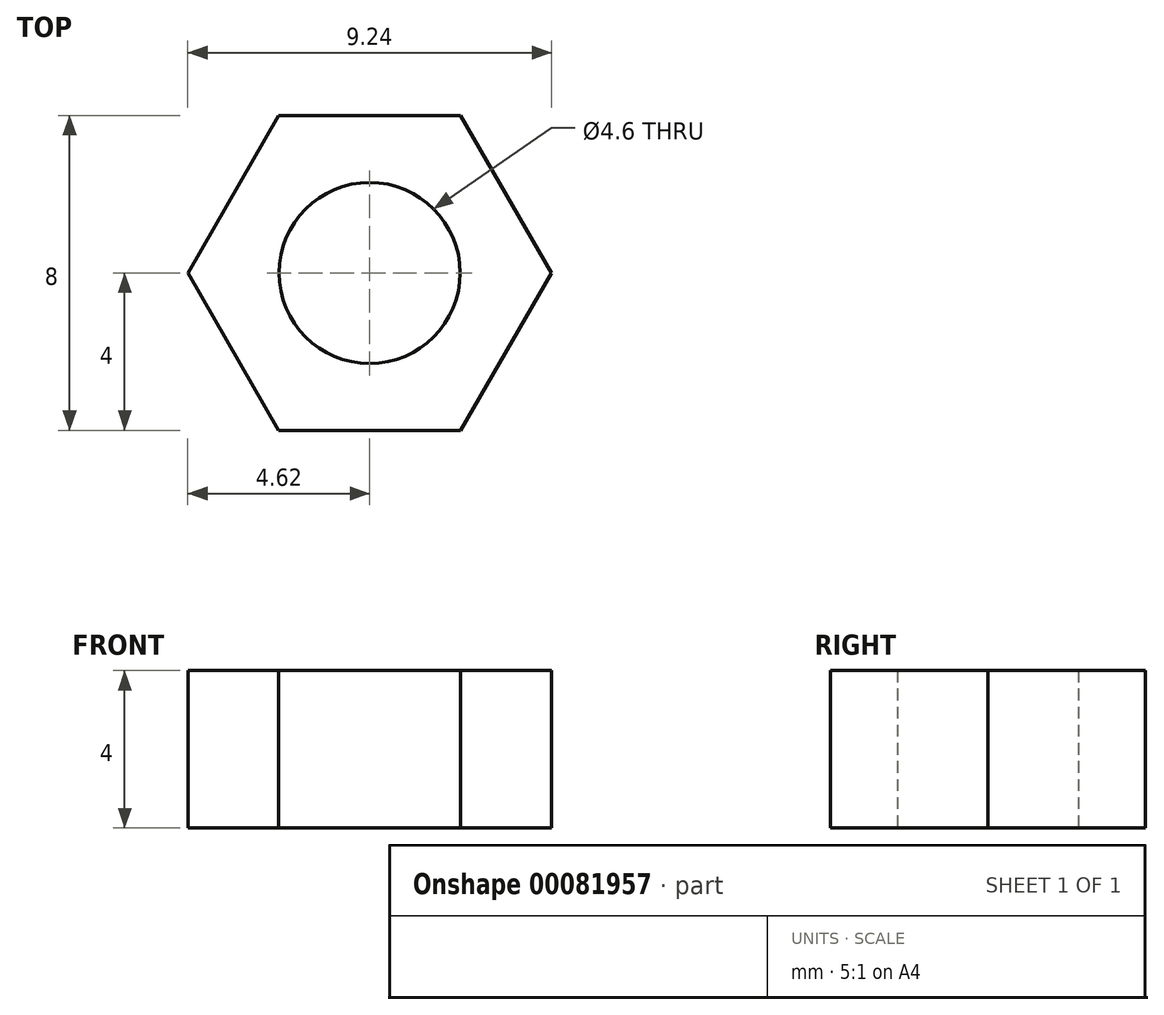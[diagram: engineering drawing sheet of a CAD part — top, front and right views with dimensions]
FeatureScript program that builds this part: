
annotation { "Feature Type Name" : "Feature", "Feature Type Description" : "" }
export const myFeature = defineFeature(function(context is Context, id is Id, definition is map)
    precondition{}
    {
        {
            assignVariable(context, id + "F0", {"name" : "NutT", "anyValue" : 4});
        }
        {
            var Q0;
            Q0=qCreatedBy(makeId("Top.planeOp"),FACE);
            var sketch = newSketch(context, id + "F1", { "sketchPlane" : qUnion([Q0])});
            skCircle(sketch, "E0.cCircle", {"center": v(0, 0) * mm, "radius": 4 * mm, "construction": true});
            skLineSegment(sketch, "E0.0", {"start": v(-4.62, 0) * mm, "end": v(-2.3, 4) * mm});
            skLineSegment(sketch, "E0.1", {"start": v(-2.3, 4) * mm, "end": v(2.3, 4) * mm});
            skLineSegment(sketch, "E0.2", {"start": v(2.3, 4) * mm, "end": v(4.62, 0) * mm});
            skLineSegment(sketch, "E0.3", {"start": v(4.62, 0) * mm, "end": v(2.3, -4) * mm});
            skLineSegment(sketch, "E0.4", {"start": v(2.3, -4) * mm, "end": v(-2.3, -4) * mm});
            skLineSegment(sketch, "E0.5", {"start": v(-2.3, -4) * mm, "end": v(-4.62, 0) * mm});
            skPoint(sketch, "E0.0.midPoint", {"position": v(-3.46, 2) * mm});
            skCircle(sketch, "E1", {"center": v(0, 0) * mm, "radius": 2.3 * mm});
            skSolve(sketch);
        }
        {
            var Q0;
            Q0=qSketchRegion(id+"F1",true);
            extrude(context, id + "F2", {"entities" : qUnion([Q0]), "depth" : (getVariable(context, 'NutT')) * mm});
        }
    });
